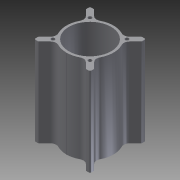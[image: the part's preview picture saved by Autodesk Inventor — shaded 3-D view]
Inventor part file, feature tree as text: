
AUTODESK INVENTOR PART (.ipt)
format: ipt  version: 2012 SP2 (Build 160219200, 219)  size: 195,584 bytes
history: native  units: mm
features: extrude x2, sketch x2
ambient origin geometry x8: Origin, YZ Plane, XZ Plane, XY Plane, X Axis, Y Axis, Z Axis, Center Point
bodies: Solid1 (feature_tree)
feature tree (4):
  extrude  "Extrusion1"  Depth=250.0mm TaperAngle=0.0deg
  extrude  "Extrusion2"  [1 undecoded]
  sketch  "Sketch1"  dims[d0=400.0mm d1=0.0mm d2=250.0mm d3=0.0mm]
  sketch  "Sketch2"
note: 1 required parameter value undecoded (feature->parameter linkage not recoverable at this tier; creation-order binding heuristic only, values carry confidence <= 0.55)
